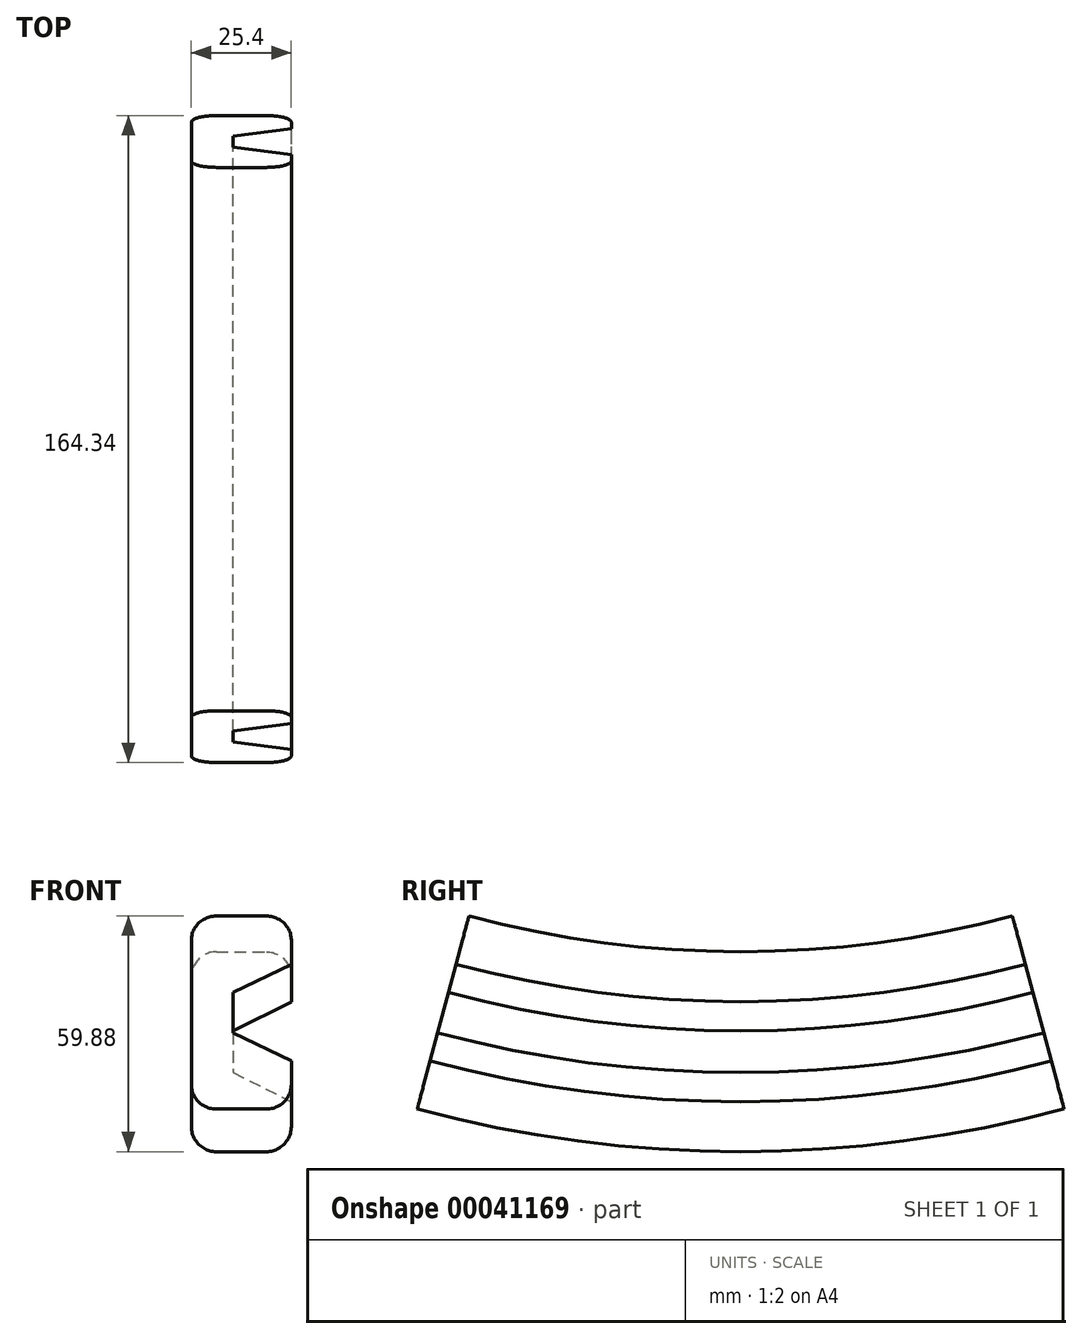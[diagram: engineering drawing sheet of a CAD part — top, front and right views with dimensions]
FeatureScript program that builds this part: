
annotation { "Feature Type Name" : "Feature", "Feature Type Description" : "" }
export const myFeature = defineFeature(function(context is Context, id is Id, definition is map)
    precondition{}
    {
        {
            var Q0;
            Q0=qCreatedBy(makeId("Front.planeOp"),FACE);
            var sketch = newSketch(context, id + "F0", { "sketchPlane" : qUnion([Q0])});
            skLineSegment(sketch, "E0", {"start": v(-49.15, 37.06) * mm, "end": v(-36.45, 37.06) * mm});
            skLineSegment(sketch, "E1", {"start": v(-44.87, 16.97) * mm, "end": v(-44.87, 6.34) * mm});
            skLineSegment(sketch, "E2", {"start": v(-55.5, 30.7) * mm, "end": v(-55.5, -7.4) * mm});
            skLineSegment(sketch, "E3", {"start": v(-49.15, -13.74) * mm, "end": v(-36.45, -13.74) * mm});
            skPoint(sketch, "E4.visualSharp", {"position": v(-55.5, 37.06) * mm});
            skArc(sketch, "E4.filletArc", {"start": v(-49.15, 37.06) * mm, "mid": v(-53.64, 35.2) * mm, "end": v(-55.5, 30.7) * mm});
            skPoint(sketch, "E5.visualSharp", {"position": v(-55.5, -13.74) * mm});
            skArc(sketch, "E5.filletArc", {"start": v(-55.5, -7.4) * mm, "mid": v(-53.64, -11.88) * mm, "end": v(-49.15, -13.74) * mm});
            skPoint(sketch, "E6.visualSharp", {"position": v(-4.7, -13.74) * mm});
            skArc(sketch, "E6.filletArc", {"start": v(-36.45, -13.74) * mm, "mid": v(-31.96, -11.88) * mm, "end": v(-30.1, -7.4) * mm});
            skPoint(sketch, "E7.visualSharp", {"position": v(-4.7, 37.06) * mm});
            skArc(sketch, "E7.filletArc", {"start": v(-30.1, 30.7) * mm, "mid": v(-31.96, 35.2) * mm, "end": v(-36.45, 37.06) * mm});
            skPoint(sketch, "E8", {"position": v(247.23, 11.66) * mm});
            skLineSegment(sketch, "E9", {"start": v(247.23, 11.66) * mm, "end": v(247.23, 0) * mm});
            skLineSegment(sketch, "E10", {"start": v(-30.1, 24.36) * mm, "end": v(-44.87, 16.97) * mm});
            skLineSegment(sketch, "E11", {"start": v(-30.1, 24.36) * mm, "end": v(-30.1, 30.7) * mm});
            skLineSegment(sketch, "E12", {"start": v(-30.1, -1.04) * mm, "end": v(-44.87, 6.34) * mm});
            skLineSegment(sketch, "E13", {"start": v(-30.1, -1.04) * mm, "end": v(-30.1, -7.4) * mm});
            skLineSegment(sketch, "E14", {"start": v(-44.87, 16.97) * mm, "end": v(-44.87, 11.66) * mm});
            skLineSegment(sketch, "E15", {"start": v(-42.8, 303.76) * mm, "end": v(-52.22, 303.76) * mm});
            skSolve(sketch);
        }
        {
            var Q0;
            Q0=makeQuery(id+"F0.imprint","IMPRINT",FACE,{"disambiguationData":[TD([[makeQuery(id+"F0.imprint","IMPRINT",EDGE,{"derivedFrom":sQuery(id+"F0.wireOp",EDGE,"E0")}),-1.0]])]});
            var Q1;
            Q1=sQuery(id+"F0.wireOp",EDGE,"E0");
            var Q2;
            Q2=sQuery(id+"F0.wireOp",EDGE,"E4.filletArc");
            var Q3;
            Q3=sQuery(id+"F0.wireOp",EDGE,"E2");
            var Q4;
            Q4=sQuery(id+"F0.wireOp",EDGE,"E7.filletArc");
            var Q5;
            Q5=sQuery(id+"F0.wireOp",EDGE,"3352df40-99eb-4d6d-ab64-4eb77467014a");
            var Q6;
            Q6=sQuery(id+"F0.wireOp",EDGE,"e21ff906-9fa8-430d-814f-205eb433ba27");
            var Q7;
            Q7=sQuery(id+"F0.wireOp",EDGE,"E1");
            var Q8;
            Q8=sQuery(id+"F0.wireOp",EDGE,"1820fb43-8a43-468b-8f48-1f127378ad0f");
            var Q9;
            Q9=sQuery(id+"F0.wireOp",EDGE,"9c30f464-c7be-41d6-a98d-f67b8ec0e6ef");
            var Q10;
            Q10=sQuery(id+"F0.wireOp",EDGE,"E6.filletArc");
            var Q11;
            Q11=sQuery(id+"F0.wireOp",EDGE,"E3");
            var Q12;
            Q12=sQuery(id+"F0.wireOp",EDGE,"E5.filletArc");
            var Q13;
            Q13=sQuery(id+"F0.wireOp",EDGE,"E15");
            revolve(context, id + "F1", {"entities" : qUnion([Q0]), "surfaceEntities" : qUnion([Q1, Q2, Q3, Q4, Q5, Q6, Q7, Q8, Q9, Q10, Q11, Q12]), "axis" : qUnion([Q13]), "revolveType" : RevolveType.SYMMETRIC, "angle" : 30 * degree});
        }
    });
